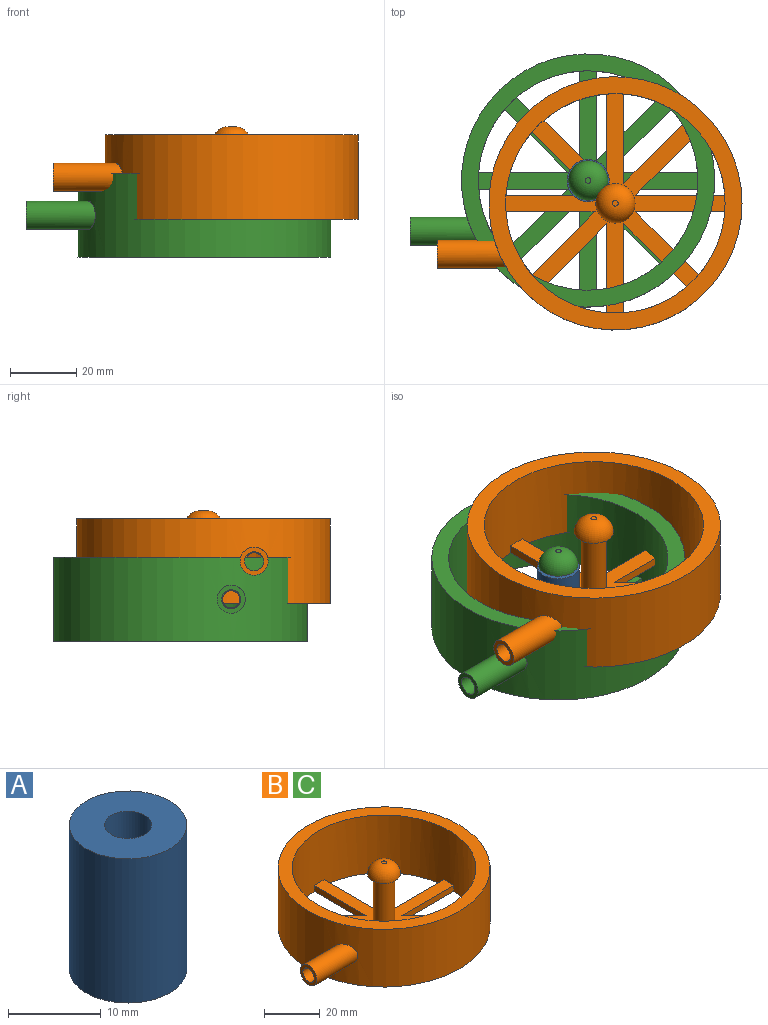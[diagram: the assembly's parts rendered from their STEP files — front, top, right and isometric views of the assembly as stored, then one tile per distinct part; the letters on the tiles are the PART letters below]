
ASSEMBLY  parts=3 mates=1
PART A: 4 faces, bbox 12.7x12.7x19.1 mm
  f0: cylinder r=2.55mm len=19.05mm, axis (0,0,-1), area 305.5mm2, adj f2,f3
  f1: cylinder r=6.35mm len=19.05mm, axis (0,0,-1), area 760.1mm2, adj f2,f3
  f2: plane 12.7x12.7mm, normal (0,0,1), area 106.2mm2, adj f0,f1
  f3: plane 12.7x12.7mm, normal (0,0,-1), area 106.2mm2, adj f0,f1
PART B: 30 faces, bbox 91.7x76.2x27.9 mm
  f0: cylinder r=38.1mm len=5.73mm, axis (0,0,-1), area 5.3mm2, adj f26,f27
  f1: cylinder r=33.02mm len=66.04mm, axis (0,0,-1), area 5141.6mm2, adj f3,f4,f5,f6,f7,f8,f9,f10
  f2: cylinder r=38.1mm len=76.2mm, axis (0,0,-1), area 6019.1mm2, adj f3,f4,f28
  f3: plane 76.2x76.2mm, normal (0,0,1), area 1135mm2, adj f1,f2
  f4: plane 76.2x76.2mm, normal (0,0,-1), area 2351mm2, adj f1,f2,f6,f7,f8,f9,f10,f11
  f5: plane 66.04x66.04mm, normal (0,0,1), area 1170.4mm2, adj f1,f6,f7,f8,f9,f10,f11,f12
  f6: plane 26.79x2.54mm, normal (-1,0,0), area 68mm2, adj f1,f4,f5,f21
  f7: plane 26.79x2.54mm, normal (1,0,0), area 68mm2, adj f1,f4,f5,f8
  f8: plane 18.94x18.94mm, normal (-0.71,0.71,0), area 68mm2, adj f1,f4,f5,f7
  f9: plane 18.94x18.94mm, normal (0.71,-0.71,0), area 68mm2, adj f1,f4,f5,f10
  f10: plane 26.79x2.54mm, normal (0,1,0), area 68mm2, adj f1,f4,f5,f9
  f11: plane 26.79x2.54mm, normal (0,-1,0), area 68mm2, adj f1,f4,f5,f12
  f12: plane 18.94x18.94mm, normal (0.71,0.71,0), area 68mm2, adj f1,f4,f5,f11
  f13: plane 18.94x18.94mm, normal (-0.71,-0.71,0), area 68mm2, adj f1,f4,f5,f14
  f14: plane 26.79x2.54mm, normal (1,0,0), area 68mm2, adj f1,f4,f5,f13
  f15: plane 26.79x2.54mm, normal (-1,0,0), area 68mm2, adj f1,f4,f5,f16
  f16: plane 18.94x18.94mm, normal (0.71,-0.71,0), area 68mm2, adj f1,f4,f5,f15
  f17: plane 18.94x18.94mm, normal (-0.71,0.71,0), area 68mm2, adj f1,f4,f5,f18
  f18: plane 26.79x2.54mm, normal (0,-1,0), area 68mm2, adj f1,f4,f5,f17
  f19: plane 26.79x2.54mm, normal (0,1,0), area 68mm2, adj f1,f4,f5,f20
  f20: plane 18.94x18.94mm, normal (-0.71,-0.71,0), area 68mm2, adj f1,f4,f5,f19
  f21: plane 18.94x18.94mm, normal (0.71,0.71,0), area 68mm2, adj f1,f4,f5,f6
  f22: cylinder r=3.81mm len=20.32mm, axis (0,0,-1), area 486.4mm2, adj f5,f24
  f23: plane 1.69x1.69mm, normal (0,0,1), area 2.2mm2, adj f25
  f24: plane 11.85x11.85mm, normal (0,0,-1), area 64.7mm2, adj f22,f25
  f25: torus R=0.84mm, axis (0,0,1), area 204.5mm2, adj f23,f24
  f26: cylinder r=2.58mm len=8.14mm, axis (1,0,0), area 91.5mm2, adj f0,f1
  f27: cylinder r=2.86mm len=20.07mm, axis (1,0,0), area 337.3mm2, adj f0,f29
  f28: cylinder r=4.22mm len=20.84mm, axis (1,0,0), area 499.4mm2, adj f2,f29
  f29: plane 8.44x8.44mm, normal (-1,0,0), area 30.2mm2, adj f27,f28
PART C: same geometry as B
PLACE A rot(axis=(0,0,1),30.7deg) t=(-16.79,12.63,0.63)mm
PLACE B t=(-8.58,5.74,8.92)mm
PLACE C t=(-16.79,12.63,-2.54)mm fixed
MATE revolute A.f0 <-> C.f22  axis (0,0,1) through (-16.79,12.63,10.16)mm
